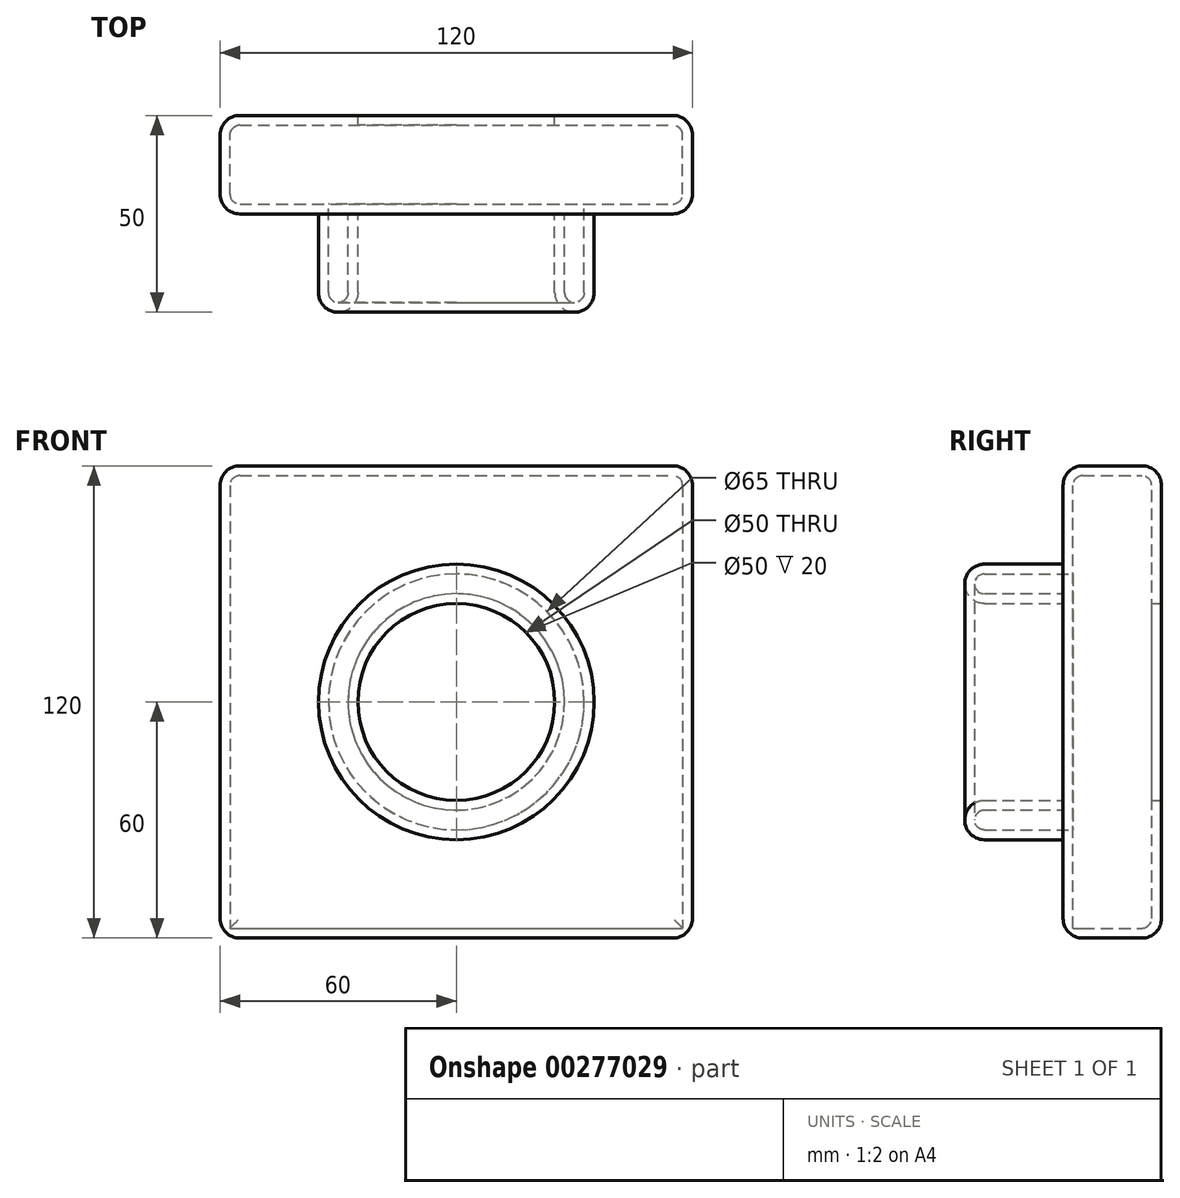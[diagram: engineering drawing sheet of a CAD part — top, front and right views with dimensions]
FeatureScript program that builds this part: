
annotation { "Feature Type Name" : "Feature", "Feature Type Description" : "" }
export const myFeature = defineFeature(function(context is Context, id is Id, definition is map)
    precondition{}
    {
        {
            var Q0;
            Q0=qCreatedBy(makeId("Front.planeOp"),FACE);
            var sketch = newSketch(context, id + "F0", { "sketchPlane" : qUnion([Q0])});
            skLineSegment(sketch, "E0.bottom", {"start": v(-60, 60) * mm, "end": v(60, 60) * mm});
            skLineSegment(sketch, "E0.top", {"start": v(-60, -60) * mm, "end": v(60, -60) * mm});
            skLineSegment(sketch, "E0.left", {"start": v(-60, 60) * mm, "end": v(-60, -60) * mm});
            skLineSegment(sketch, "E0.right", {"start": v(60, 60) * mm, "end": v(60, -60) * mm});
            skPoint(sketch, "E0.middle", {"position": v(0, 0) * mm});
            skSolve(sketch);
        }
        {
            var Q0;
            Q0 = qSketchRegion(id + "F0", true);
            extrude(context, id + "F1", {"entities" : qUnion([Q0]), "depth" : 25 * mm});
        }
        {
            var Q0;
            Q0=makeQuery(id+"F1.opExtrude","CAP_FACE",FACE,{"disambiguationData":[OSD([sQuery(id+"F0.wireOp",EDGE,"E0.bottom"),sQuery(id+"F0.wireOp",EDGE,"E0.top"),sQuery(id+"F0.wireOp",EDGE,"E0.left"),sQuery(id+"F0.wireOp",EDGE,"E0.right")])],"isStart":false});
            var sketch = newSketch(context, id + "F2", { "sketchPlane" : qUnion([Q0])});
            skCircle(sketch, "E1", {"center": v(0, 0) * mm, "radius": 25 * mm});
            skCircle(sketch, "E2", {"center": v(0, 0) * mm, "radius": 35 * mm});
            skSolve(sketch);
        }
        {
            var Q0;
            Q0 = qSketchRegion(id + "F2", true);
            extrude(context, id + "F3", {"entities" : qUnion([Q0]), "operationType" : NewBodyOperationType.ADD, "depth" : 25 * mm});
        }
        {
            var Q0;
            Q0=makeQuery(id+"F1.opExtrude","CAP_EDGE",EDGE,{"disambiguationData":[OSD([sQuery(id+"F0.wireOp",EDGE,"E0.bottom")])],"isStart":false});
            var Q1;
            Q1=makeQuery(id+"F1.opExtrude","CAP_EDGE",EDGE,{"disambiguationData":[OSD([sQuery(id+"F0.wireOp",EDGE,"E0.left")])],"isStart":false});
            var Q2;
            Q2=makeQuery(id+"F1.opExtrude","CAP_EDGE",EDGE,{"disambiguationData":[OSD([sQuery(id+"F0.wireOp",EDGE,"E0.bottom")])],"isStart":true});
            var Q3;
            Q3=makeQuery(id+"F1.opExtrude","CAP_EDGE",EDGE,{"disambiguationData":[OSD([sQuery(id+"F0.wireOp",EDGE,"E0.right")])],"isStart":false});
            var Q4;
            Q4=makeQuery(id+"F1.opExtrude","CAP_EDGE",EDGE,{"disambiguationData":[OSD([sQuery(id+"F0.wireOp",EDGE,"E0.right")])],"isStart":true});
            var Q5;
            Q5=makeQuery(id+"F1.opExtrude","CAP_EDGE",EDGE,{"disambiguationData":[OSD([sQuery(id+"F0.wireOp",EDGE,"E0.top")])],"isStart":true});
            var Q6;
            Q6=makeQuery(id+"F1.opExtrude","CAP_EDGE",EDGE,{"disambiguationData":[OSD([sQuery(id+"F0.wireOp",EDGE,"E0.left")])],"isStart":true});
            var Q7;
            Q7=makeQuery(id+"F1.opExtrude","SWEPT_EDGE",EDGE,{"disambiguationData":[OSD([sQuery(id+"F0.wireOp",EDGE,"E0.bottom"),sQuery(id+"F0.wireOp",EDGE,"E0.left")])]});
            var Q8;
            Q8=makeQuery(id+"F1.opExtrude","SWEPT_EDGE",EDGE,{"disambiguationData":[OSD([sQuery(id+"F0.wireOp",EDGE,"E0.bottom"),sQuery(id+"F0.wireOp",EDGE,"E0.right")])]});
            var Q9;
            Q9=makeQuery(id+"F3.opExtrude","CAP_EDGE",EDGE,{"disambiguationData":[OSD([sQuery(id+"F2.wireOp",EDGE,"E2")])],"isStart":true});
            var Q10;
            Q10=makeQuery(id+"F3.opExtrude","CAP_EDGE",EDGE,{"disambiguationData":[OSD([sQuery(id+"F2.wireOp",EDGE,"E1")])],"isStart":false});
            var Q11;
            Q11=makeQuery(id+"F3.opExtrude","CAP_EDGE",EDGE,{"disambiguationData":[OSD([sQuery(id+"F2.wireOp",EDGE,"E2")])],"isStart":false});
            fillet(context, id + "F4", {"entities" : qUnion([Q0, Q1, Q2, Q3, Q4, Q5, Q6, Q7, Q8, Q9, Q10, Q11]), "radius" : 5 * mm, "tangentPropagation" : true, "allowEdgeOverflow" : false});
        }
        {
            var Q0;
            Q0=makeQuery(id+"F3.boolean.opBoolean","SPLIT",FACE,{"disambiguationData":[TD([makeQuery(id+"F3.opExtrude","SWEPT_FACE",FACE,{"disambiguationData":[OSD([sQuery(id+"F2.wireOp",EDGE,"E1")])]})])],"derivedFrom":makeQuery(id+"F1.opExtrude","CAP_FACE",FACE,{"disambiguationData":[OSD([sQuery(id+"F0.wireOp",EDGE,"E0.bottom"),sQuery(id+"F0.wireOp",EDGE,"E0.top"),sQuery(id+"F0.wireOp",EDGE,"E0.left"),sQuery(id+"F0.wireOp",EDGE,"E0.right")])],"isStart":false})});
            shell(context, id + "F5", {"entities" : qUnion([Q0]), "thickness" : 2.5 * mm});
        }
        {
            var Q0;
            {var subQ0=sQuery(id+"F0.wireOp",EDGE,"E0.right");var subQ1=sQuery(id+"F0.wireOp",EDGE,"E0.left");var subQ2=sQuery(id+"F0.wireOp",EDGE,"E0.top");var subQ3=sQuery(id+"F0.wireOp",EDGE,"E0.bottom");Q0=makeQuery(id+"F5.opShell","OFFSET_FACE",FACE,{"disambiguationData":[OSD([subQ3,subQ2,subQ1,subQ0]),TDD([makeQuery(id+"F1.opExtrude","CAP_FACE",FACE,{"disambiguationData":[OSD([subQ3,subQ2,subQ1,subQ0])],"isStart":true})])]});}
            var sketch = newSketch(context, id + "F6", { "sketchPlane" : qUnion([Q0])});
            skCircle(sketch, "E3", {"center": v(0, 0) * mm, "radius": 25 * mm});
            skSolve(sketch);
        }
        {
            var Q0;
            Q0 = qSketchRegion(id + "F6", true);
            extrude(context, id + "F7", {"entities" : qUnion([Q0]), "operationType" : NewBodyOperationType.ADD, "depth" : 25 * mm});
        }
        {
            var Q0;
            Q0=makeQuery(id+"F1.opExtrude","CAP_FACE",FACE,{"disambiguationData":[OSD([sQuery(id+"F0.wireOp",EDGE,"E0.bottom"),sQuery(id+"F0.wireOp",EDGE,"E0.top"),sQuery(id+"F0.wireOp",EDGE,"E0.left"),sQuery(id+"F0.wireOp",EDGE,"E0.right")])],"isStart":true});
            var sketch = newSketch(context, id + "F8", { "sketchPlane" : qUnion([Q0])});
            skCircle(sketch, "E4", {"center": v(0, 0) * mm, "radius": 25 * mm});
            skCircle(sketch, "E5", {"center": v(0, 0) * mm, "radius": 35 * mm});
            skSolve(sketch);
        }
        {
            var Q0;
            Q0=makeQuery(id+"F8.imprint","IMPRINT",FACE,{"disambiguationData":[TD([[makeQuery(id+"F8.imprint","IMPRINT",EDGE,{"derivedFrom":sQuery(id+"F8.wireOp",EDGE,"E4")}),1.0]])]});
            extrude(context, id + "F9", {"entities" : qUnion([Q0]), "operationType" : NewBodyOperationType.REMOVE, "oppositeDirection" : true, "depth" : 99.8 * mm});
        }
        {
            var Q0;
            Q0=makeQuery(id+"F1.opExtrude","CAP_EDGE",EDGE,{"disambiguationData":[OSD([sQuery(id+"F0.wireOp",EDGE,"E0.top")])],"isStart":false});
            fillet(context, id + "F10", {"entities" : qUnion([Q0]), "radius" : 5 * mm, "tangentPropagation" : true, "allowEdgeOverflow" : false});
        }
        {
            var Q0;
            Q0=makeQuery(id+"F1.opExtrude","CAP_FACE",FACE,{"disambiguationData":[OSD([sQuery(id+"F0.wireOp",EDGE,"E0.bottom"),sQuery(id+"F0.wireOp",EDGE,"E0.top"),sQuery(id+"F0.wireOp",EDGE,"E0.left"),sQuery(id+"F0.wireOp",EDGE,"E0.right")])],"isStart":true});
            shell(context, id + "F11", {"entities" : qUnion([Q0]), "thickness" : 2.5 * mm});
        }
    });
